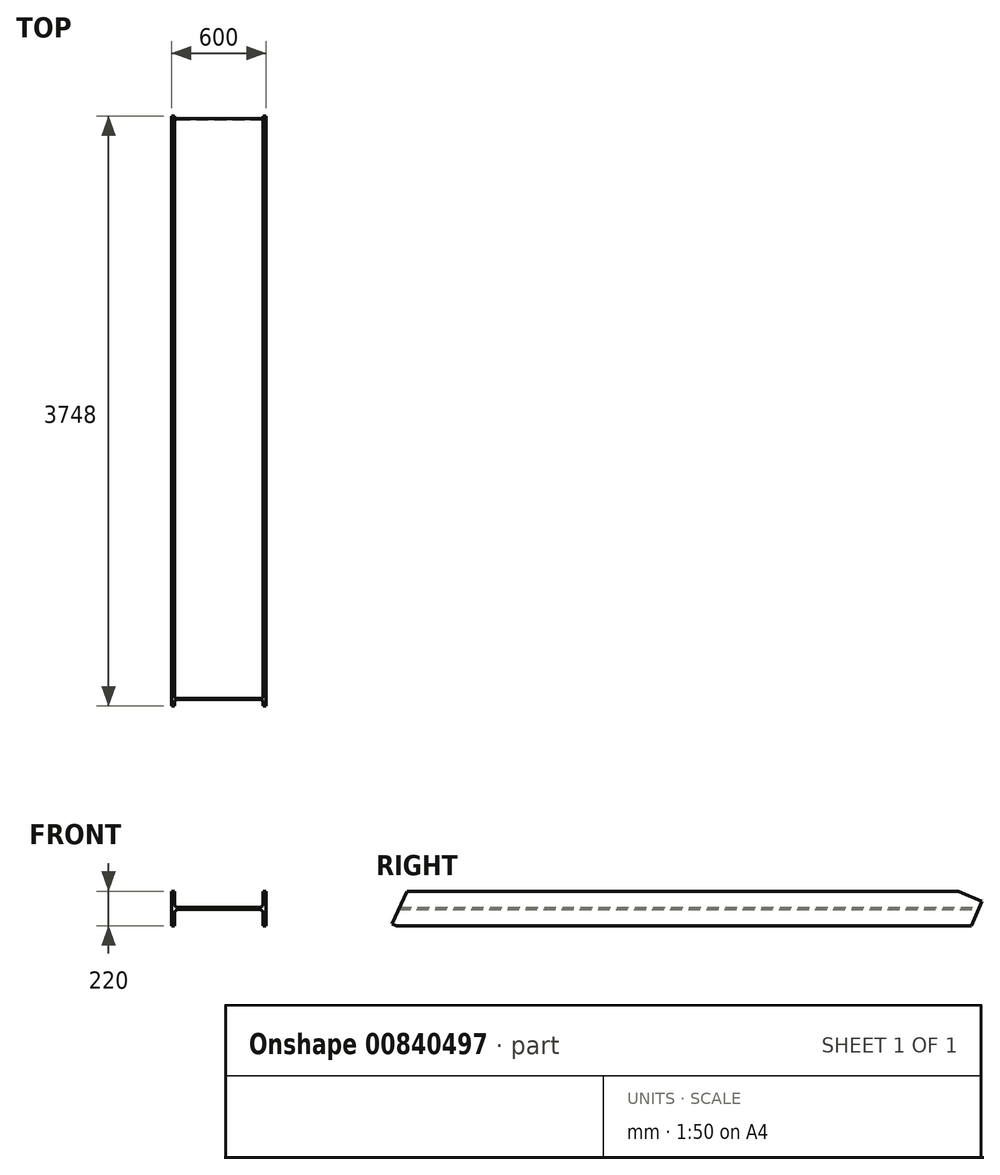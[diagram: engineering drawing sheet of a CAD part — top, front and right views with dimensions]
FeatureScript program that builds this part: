
annotation { "Feature Type Name" : "Feature", "Feature Type Description" : "" }
export const myFeature = defineFeature(function(context is Context, id is Id, definition is map)
    precondition{}
    {
        {
            var Q0;
            Q0=qCreatedBy(makeId("Front.planeOp"),FACE);
            var sketch = newSketch(context, id + "F0", { "sketchPlane" : qUnion([Q0])});
            skLineSegment(sketch, "E0", {"start": v(0, 6) * mm, "end": v(-257, 6) * mm});
            skLineSegment(sketch, "E1", {"start": v(-281, 30) * mm, "end": v(-281, 110) * mm});
            skLineSegment(sketch, "E2", {"start": v(-281, 110) * mm, "end": v(-300, 110) * mm});
            skLineSegment(sketch, "E3", {"start": v(-300, 110) * mm, "end": v(-300, 0) * mm});
            skLineSegment(sketch, "E4", {"start": v(-300, 0) * mm, "end": v(0, 0) * mm, "construction": true});
            skLineSegment(sketch, "E5", {"start": v(0, 0) * mm, "end": v(0, 379.86) * mm, "construction": true});
            skPoint(sketch, "E6.visualSharp", {"position": v(-281, 6) * mm});
            skArc(sketch, "E6.filletArc", {"start": v(-281, 30) * mm, "mid": v(-273.97, 13.03) * mm, "end": v(-257, 6) * mm});
            skLineSegment(sketch, "E7.MirrorCS", {"start": v(-281, -110) * mm, "end": v(-300, -110) * mm});
            skArc(sketch, "E8.MirrorCS", {"start": v(-281, -30) * mm, "mid": v(-273.97, -13.03) * mm, "end": v(-257, -6) * mm});
            skLineSegment(sketch, "E9.MirrorCS", {"start": v(0, -6) * mm, "end": v(-257, -6) * mm});
            skPoint(sketch, "E10.MirrorP", {"position": v(-281, -6) * mm});
            skLineSegment(sketch, "E11.MirrorCS", {"start": v(-281, -30) * mm, "end": v(-281, -110) * mm});
            skLineSegment(sketch, "E12.MirrorCS", {"start": v(-300, -110) * mm, "end": v(-300, 0) * mm});
            skLineSegment(sketch, "E13.MirrorCS", {"start": v(281, 110) * mm, "end": v(300, 110) * mm});
            skLineSegment(sketch, "E14.MirrorCS", {"start": v(281, -110) * mm, "end": v(300, -110) * mm});
            skArc(sketch, "E15.MirrorCS", {"start": v(281, -30) * mm, "mid": v(273.97, -13.03) * mm, "end": v(257, -6) * mm});
            skArc(sketch, "E16.MirrorCS", {"start": v(281, 30) * mm, "mid": v(273.97, 13.03) * mm, "end": v(257, 6) * mm});
            skLineSegment(sketch, "E17.MirrorCS", {"start": v(300, 0) * mm, "end": v(0, 0) * mm, "construction": true});
            skLineSegment(sketch, "E18.MirrorCS", {"start": v(281, -30) * mm, "end": v(281, -110) * mm});
            skLineSegment(sketch, "E19.MirrorCS", {"start": v(300, -110) * mm, "end": v(300, 0) * mm});
            skLineSegment(sketch, "E20.MirrorCS", {"start": v(300, 110) * mm, "end": v(300, 0) * mm});
            skLineSegment(sketch, "E21.MirrorCS", {"start": v(0, 6) * mm, "end": v(257, 6) * mm});
            skPoint(sketch, "E22.MirrorP", {"position": v(281, 6) * mm});
            skLineSegment(sketch, "E23.MirrorCS", {"start": v(0, -6) * mm, "end": v(257, -6) * mm});
            skLineSegment(sketch, "E24.MirrorCS", {"start": v(281, 30) * mm, "end": v(281, 110) * mm});
            skPoint(sketch, "E25.MirrorP", {"position": v(281, -6) * mm});
            skSolve(sketch);
        }
        {
            var Q0;
            Q0 = qSketchRegion(id + "F0", true);
            extrude(context, id + "F1", {"entities" : qUnion([Q0]), "depth" : 4000 * mm, "offsetDistance" : 25 * mm});
        }
        {
            var Q0;
            Q0=makeQuery(id+"F1.opExtrude","SWEPT_FACE",FACE,{"disambiguationData":[OSD([sQuery(id+"F0.wireOp",EDGE,"E19.MirrorCS"),sQuery(id+"F0.wireOp",EDGE,"E20.MirrorCS")])]});
            var sketch = newSketch(context, id + "F2", { "sketchPlane" : qUnion([Q0])});
            skLineSegment(sketch, "E26", {"start": v(-3972, -110) * mm, "end": v(-4000, -99) * mm});
            skLineSegment(sketch, "E27", {"start": v(-4000, -99) * mm, "end": v(-3905, 110) * mm});
            skLineSegment(sketch, "E28", {"start": v(-3905, 110) * mm, "end": v(-4000, 110) * mm});
            skLineSegment(sketch, "E29", {"start": v(-4000, 110) * mm, "end": v(-4000, -110) * mm});
            skLineSegment(sketch, "E30", {"start": v(-4000, -110) * mm, "end": v(-3972, -110) * mm});
            skLineSegment(sketch, "E31", {"start": v(-319, -110) * mm, "end": v(-252, 46) * mm});
            skLineSegment(sketch, "E32", {"start": v(-252, 46) * mm, "end": v(-401.01, 110) * mm});
            skLineSegment(sketch, "E33", {"start": v(-401.01, 110) * mm, "end": v(0, 110) * mm});
            skLineSegment(sketch, "E34", {"start": v(0, 110) * mm, "end": v(0, -110) * mm});
            skLineSegment(sketch, "E35", {"start": v(0, -110) * mm, "end": v(-319, -110) * mm});
            skSolve(sketch);
        }
        {
            var Q0;
            Q0 = qSketchRegion(id + "F2", true);
            extrude(context, id + "F3", {"entities" : qUnion([Q0]), "operationType" : NewBodyOperationType.REMOVE, "endBound" : BoundingType.THROUGH_ALL, "oppositeDirection" : true, "depth" : 25 * mm, "offsetDistance" : 25 * mm});
        }
    });
